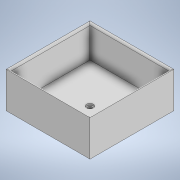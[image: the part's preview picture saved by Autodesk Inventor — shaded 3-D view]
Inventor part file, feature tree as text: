
AUTODESK INVENTOR PART (.ipt)
format: ipt  version: 2020.3 (Build 243373000, 373)  size: 123,392 bytes
history: native  units: mm
features: extrude x4, sketch x4, fillet x1
ambient origin geometry x8: Origin, YZ Plane, XZ Plane, XY Plane, X Axis, Y Axis, Z Axis, Center Point
bodies: Solid1 (feature_tree)
feature tree (9):
  extrude  "Extrusion1"  Depth=5.0mm TaperAngle=0.0deg
  extrude  "Extrusion2"  Depth=5.0mm
  fillet  "Fillet1"  Radius=10.0mm
  extrude  "Extrusion3"  Depth=2.0mm TaperAngle=0.0deg
  extrude  "Extrusion4"  [1 undecoded]
  sketch  "Sketch1"  dims[d3=5.0mm d4=0.0mm d9=40.0mm d10=0.0mm]
  sketch  "Sketch4"  dims[d11=2.5mm d12=5.0mm d13=10.0mm d14=0.0mm]
  sketch  "Sketch5"  dims[d15=8.5mm d16=2.0mm d17=0.0mm]
  sketch  "Sketch6"
note: 1 required parameter value undecoded (feature->parameter linkage not recoverable at this tier; creation-order binding heuristic only, values carry confidence <= 0.55)
